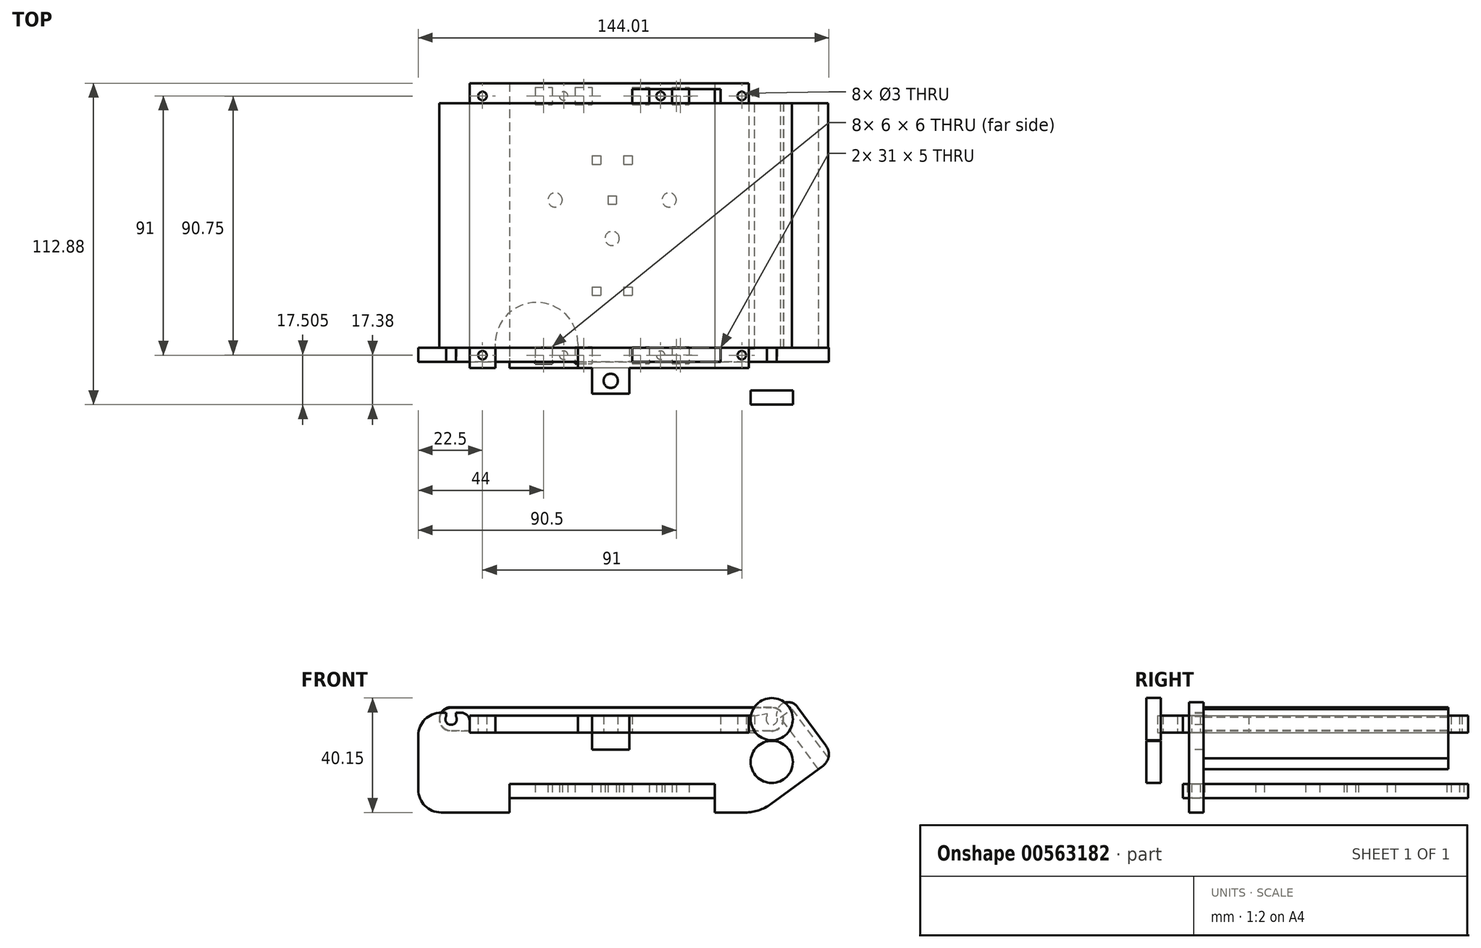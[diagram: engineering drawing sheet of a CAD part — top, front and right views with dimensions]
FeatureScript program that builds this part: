
annotation { "Feature Type Name" : "Feature", "Feature Type Description" : "" }
export const myFeature = defineFeature(function(context is Context, id is Id, definition is map)
    precondition{}
    {
        {
            var Q0;
            Q0=qCreatedBy(makeId("Top.planeOp"),FACE);
            var sketch = newSketch(context, id + "F0", { "sketchPlane" : qUnion([Q0])});
            skLineSegment(sketch, "E0.bottom", {"start": v(36, 50) * mm, "end": v(-36, 50) * mm});
            skLineSegment(sketch, "E0.top", {"start": v(36, -50) * mm, "end": v(-36, -50) * mm});
            skLineSegment(sketch, "E0.left", {"start": v(36, 50) * mm, "end": v(36, -50) * mm});
            skLineSegment(sketch, "E0.right", {"start": v(-36, 50) * mm, "end": v(-36, -50) * mm});
            skPoint(sketch, "E0.middle", {"position": v(0, 0) * mm});
            skLineSegment(sketch, "E1.bottom", {"start": v(-27, -42.5) * mm, "end": v(-21, -42.5) * mm});
            skLineSegment(sketch, "E1.top", {"start": v(-27, -48.5) * mm, "end": v(-21, -48.5) * mm});
            skLineSegment(sketch, "E1.left", {"start": v(-27, -42.5) * mm, "end": v(-27, -48.5) * mm});
            skLineSegment(sketch, "E1.right", {"start": v(-21, -42.5) * mm, "end": v(-21, -48.5) * mm});
            skLineSegment(sketch, "E2.bottom", {"start": v(-13, -42.5) * mm, "end": v(-7, -42.5) * mm});
            skLineSegment(sketch, "E2.top", {"start": v(-13, -48.5) * mm, "end": v(-7, -48.5) * mm});
            skLineSegment(sketch, "E2.left", {"start": v(-13, -42.5) * mm, "end": v(-13, -48.5) * mm});
            skLineSegment(sketch, "E2.right", {"start": v(-7, -42.5) * mm, "end": v(-7, -48.5) * mm});
            skLineSegment(sketch, "E3", {"start": v(-21, -45.5) * mm, "end": v(-17, -45.5) * mm, "construction": true});
            skLineSegment(sketch, "E4", {"start": v(-17, -45.5) * mm, "end": v(-13, -45.5) * mm, "construction": true});
            skCircle(sketch, "E5", {"center": v(-17, -45.5) * mm, "radius": 1.5 * mm});
            skLineSegment(sketch, "E6.bottom", {"start": v(-27, 48.5) * mm, "end": v(-21, 48.5) * mm});
            skLineSegment(sketch, "E6.top", {"start": v(-27, 42.5) * mm, "end": v(-21, 42.5) * mm});
            skLineSegment(sketch, "E6.left", {"start": v(-27, 48.5) * mm, "end": v(-27, 42.5) * mm});
            skLineSegment(sketch, "E6.right", {"start": v(-21, 48.5) * mm, "end": v(-21, 42.5) * mm});
            skLineSegment(sketch, "E7.bottom", {"start": v(-13, 48.5) * mm, "end": v(-7, 48.5) * mm});
            skLineSegment(sketch, "E7.top", {"start": v(-13, 42.5) * mm, "end": v(-7, 42.5) * mm});
            skLineSegment(sketch, "E7.left", {"start": v(-13, 48.5) * mm, "end": v(-13, 42.5) * mm});
            skLineSegment(sketch, "E7.right", {"start": v(-7, 48.5) * mm, "end": v(-7, 42.5) * mm});
            skLineSegment(sketch, "E8.bottom", {"start": v(7, 48.5) * mm, "end": v(13, 48.5) * mm});
            skLineSegment(sketch, "E8.top", {"start": v(7, 42.5) * mm, "end": v(13, 42.5) * mm});
            skLineSegment(sketch, "E8.left", {"start": v(7, 48.5) * mm, "end": v(7, 42.5) * mm});
            skLineSegment(sketch, "E8.right", {"start": v(13, 48.5) * mm, "end": v(13, 42.5) * mm});
            skLineSegment(sketch, "E9.bottom", {"start": v(21, 48.5) * mm, "end": v(27, 48.5) * mm});
            skLineSegment(sketch, "E9.top", {"start": v(21, 42.5) * mm, "end": v(27, 42.5) * mm});
            skLineSegment(sketch, "E9.left", {"start": v(21, 48.5) * mm, "end": v(21, 42.5) * mm});
            skLineSegment(sketch, "E9.right", {"start": v(27, 48.5) * mm, "end": v(27, 42.5) * mm});
            skLineSegment(sketch, "E10.bottom", {"start": v(7, -42.5) * mm, "end": v(13, -42.5) * mm});
            skLineSegment(sketch, "E10.top", {"start": v(7, -48.5) * mm, "end": v(13, -48.5) * mm});
            skLineSegment(sketch, "E10.left", {"start": v(7, -42.5) * mm, "end": v(7, -48.5) * mm});
            skLineSegment(sketch, "E10.right", {"start": v(13, -42.5) * mm, "end": v(13, -48.5) * mm});
            skLineSegment(sketch, "E11.bottom", {"start": v(21, -42.5) * mm, "end": v(27, -42.5) * mm});
            skLineSegment(sketch, "E11.top", {"start": v(21, -48.5) * mm, "end": v(27, -48.5) * mm});
            skLineSegment(sketch, "E11.left", {"start": v(21, -42.5) * mm, "end": v(21, -48.5) * mm});
            skLineSegment(sketch, "E11.right", {"start": v(27, -42.5) * mm, "end": v(27, -48.5) * mm});
            skLineSegment(sketch, "E12", {"start": v(-21, 45.5) * mm, "end": v(-17, 45.5) * mm, "construction": true});
            skLineSegment(sketch, "E13", {"start": v(-17, 45.5) * mm, "end": v(-13, 45.5) * mm, "construction": true});
            skLineSegment(sketch, "E14", {"start": v(13, 45.5) * mm, "end": v(17, 45.5) * mm, "construction": true});
            skLineSegment(sketch, "E15", {"start": v(17, 45.5) * mm, "end": v(21, 45.5) * mm, "construction": true});
            skLineSegment(sketch, "E16", {"start": v(13, -45.5) * mm, "end": v(17, -45.5) * mm, "construction": true});
            skLineSegment(sketch, "E17", {"start": v(17, -45.5) * mm, "end": v(21, -45.5) * mm, "construction": true});
            skLineSegment(sketch, "E18", {"start": v(0, 0) * mm, "end": v(36, 0) * mm, "construction": true});
            skLineSegment(sketch, "E19", {"start": v(0, 0) * mm, "end": v(0, 50) * mm, "construction": true});
            skCircle(sketch, "E20", {"center": v(-17, 45.5) * mm, "radius": 1.5 * mm});
            skCircle(sketch, "E21", {"center": v(17, 45.5) * mm, "radius": 1.5 * mm});
            skCircle(sketch, "E22", {"center": v(17, -45.5) * mm, "radius": 1.5 * mm});
            skCircle(sketch, "E23", {"center": v(0, -4.5) * mm, "radius": 2.5 * mm});
            skCircle(sketch, "E24", {"center": v(20, 9) * mm, "radius": 2.5 * mm});
            skCircle(sketch, "E25", {"center": v(-20, 9) * mm, "radius": 2.5 * mm});
            skLineSegment(sketch, "E26", {"start": v(0, -4.5) * mm, "end": v(-20, 9) * mm, "construction": true});
            skLineSegment(sketch, "E27", {"start": v(20, 9) * mm, "end": v(-20, 9) * mm, "construction": true});
            skLineSegment(sketch, "E28", {"start": v(20, 9) * mm, "end": v(0, -4.5) * mm, "construction": true});
            skPoint(sketch, "E29", {"position": v(0, 9) * mm});
            skLineSegment(sketch, "E30.bottom", {"start": v(-7, -21.5) * mm, "end": v(-4, -21.5) * mm});
            skLineSegment(sketch, "E30.top", {"start": v(-7, -24.5) * mm, "end": v(-4, -24.5) * mm});
            skLineSegment(sketch, "E30.left", {"start": v(-7, -21.5) * mm, "end": v(-7, -24.5) * mm});
            skLineSegment(sketch, "E30.right", {"start": v(-4, -21.5) * mm, "end": v(-4, -24.5) * mm});
            skLineSegment(sketch, "E31.bottom", {"start": v(4, -21.5) * mm, "end": v(7, -21.5) * mm});
            skLineSegment(sketch, "E31.top", {"start": v(4, -24.5) * mm, "end": v(7, -24.5) * mm});
            skLineSegment(sketch, "E31.left", {"start": v(4, -21.5) * mm, "end": v(4, -24.5) * mm});
            skLineSegment(sketch, "E31.right", {"start": v(7, -21.5) * mm, "end": v(7, -24.5) * mm});
            skLineSegment(sketch, "E32.bottom", {"start": v(-1.5, 10.5) * mm, "end": v(1.5, 10.5) * mm});
            skLineSegment(sketch, "E32.top", {"start": v(-1.5, 7.5) * mm, "end": v(1.5, 7.5) * mm});
            skLineSegment(sketch, "E32.left", {"start": v(-1.5, 10.5) * mm, "end": v(-1.5, 7.5) * mm});
            skLineSegment(sketch, "E32.right", {"start": v(1.5, 10.5) * mm, "end": v(1.5, 7.5) * mm});
            skLineSegment(sketch, "E33.bottom", {"start": v(-7, 24.5) * mm, "end": v(-4, 24.5) * mm});
            skLineSegment(sketch, "E33.top", {"start": v(-7, 21.5) * mm, "end": v(-4, 21.5) * mm});
            skLineSegment(sketch, "E33.left", {"start": v(-7, 24.5) * mm, "end": v(-7, 21.5) * mm});
            skLineSegment(sketch, "E33.right", {"start": v(-4, 24.5) * mm, "end": v(-4, 21.5) * mm});
            skLineSegment(sketch, "E34.bottom", {"start": v(4, 24.5) * mm, "end": v(7, 24.5) * mm});
            skLineSegment(sketch, "E34.top", {"start": v(4, 21.5) * mm, "end": v(7, 21.5) * mm});
            skLineSegment(sketch, "E34.left", {"start": v(4, 24.5) * mm, "end": v(4, 21.5) * mm});
            skLineSegment(sketch, "E34.right", {"start": v(7, 24.5) * mm, "end": v(7, 21.5) * mm});
            skSolve(sketch);
        }
        {
            var Q0;
            Q0=makeQuery(id+"F0.imprint","IMPRINT",FACE,{"disambiguationData":[TD([[makeQuery(id+"F0.imprint","IMPRINT",EDGE,{"derivedFrom":sQuery(id+"F0.wireOp",EDGE,"E0.bottom")}),1.0]])]});
            extrude(context, id + "F1", {"entities" : qUnion([Q0]), "depth" : 5 * mm, "offsetDistance" : 25 * mm});
        }
        {
            var Q0;
            Q0=qCreatedBy(makeId("Top.planeOp"),FACE);
            cPlane(context, id + "F2", {"entities" : qUnion([Q0]), "cplaneType" : CPlaneType.OFFSET, "offset" : 23 * mm, "width" : 150 * mm, "height" : 150 * mm});
        }
        {
            var Q0;
            Q0=qCreatedBy(id+"F2.planeOp",FACE);
            var sketch = newSketch(context, id + "F3", { "sketchPlane" : qUnion([Q0])});
            skLineSegment(sketch, "E35.bottom", {"start": v(-50, -50) * mm, "end": v(-41, -50) * mm});
            skLineSegment(sketch, "E35.top", {"start": v(-50, 50) * mm, "end": v(48, 50) * mm});
            skLineSegment(sketch, "E35.left", {"start": v(-50, -50) * mm, "end": v(-50, 50) * mm});
            skLineSegment(sketch, "E35.right", {"start": v(50, -43) * mm, "end": v(50, 43) * mm});
            skPoint(sketch, "E35.middle", {"position": v(0, 0) * mm});
            skLineSegment(sketch, "E36.bottom", {"start": v(-45.5, -45.5) * mm, "end": v(45.5, -45.5) * mm, "construction": true});
            skLineSegment(sketch, "E36.top", {"start": v(-45.5, 45.5) * mm, "end": v(45.5, 45.5) * mm, "construction": true});
            skLineSegment(sketch, "E36.left", {"start": v(-45.5, -45.5) * mm, "end": v(-45.5, 45.5) * mm, "construction": true});
            skLineSegment(sketch, "E36.right", {"start": v(45.5, -45.5) * mm, "end": v(45.5, 45.5) * mm, "construction": true});
            skCircle(sketch, "E37", {"center": v(-45.5, -45.5) * mm, "radius": 1.5 * mm});
            skCircle(sketch, "E38", {"center": v(-45.5, 45.5) * mm, "radius": 1.5 * mm});
            skCircle(sketch, "E39", {"center": v(45.5, -45.5) * mm, "radius": 1.5 * mm});
            skCircle(sketch, "E40", {"center": v(45.5, 45.5) * mm, "radius": 1.5 * mm});
            skLineSegment(sketch, "E41.bottom", {"start": v(7, -47.87) * mm, "end": v(38, -47.88) * mm});
            skLineSegment(sketch, "E41.top", {"start": v(7, -42.87) * mm, "end": v(38, -42.88) * mm});
            skLineSegment(sketch, "E41.left", {"start": v(7, -47.88) * mm, "end": v(7, -42.88) * mm});
            skLineSegment(sketch, "E41.right", {"start": v(38, -47.88) * mm, "end": v(38, -42.88) * mm});
            skLineSegment(sketch, "E42.bottom", {"start": v(7, 42.88) * mm, "end": v(38, 42.88) * mm});
            skLineSegment(sketch, "E42.top", {"start": v(7, 47.88) * mm, "end": v(38, 47.88) * mm});
            skLineSegment(sketch, "E42.left", {"start": v(7, 42.88) * mm, "end": v(7, 47.88) * mm});
            skLineSegment(sketch, "E42.right", {"start": v(38, 42.88) * mm, "end": v(38, 47.88) * mm});
            skLineSegment(sketch, "E43", {"start": v(45.5, 0) * mm, "end": v(-45.5, 0) * mm, "construction": true});
            skLineSegment(sketch, "E44", {"start": v(-41, -50) * mm, "end": v(-41, -41.5) * mm});
            skLineSegment(sketch, "E45", {"start": v(-41, -41.5) * mm, "end": v(-12, -41.5) * mm, "construction": true});
            skLineSegment(sketch, "E46", {"start": v(-12, -41.5) * mm, "end": v(-12, -50) * mm});
            skArc(sketch, "E47", {"start": v(-12, -41.5) * mm, "mid": v(-26.5, -27) * mm, "end": v(-41, -41.5) * mm});
            skLineSegment(sketch, "E48.trimOffspring", {"start": v(-12, -50) * mm, "end": v(-7, -50) * mm});
            skLineSegment(sketch, "E49", {"start": v(-7, -59) * mm, "end": v(6, -59) * mm});
            skLineSegment(sketch, "E50", {"start": v(6, -59) * mm, "end": v(6, -50) * mm});
            skLineSegment(sketch, "E51.trimOffspring", {"start": v(6, -50) * mm, "end": v(48, -50) * mm});
            skLineSegment(sketch, "E52", {"start": v(-7, -59) * mm, "end": v(-7, -50) * mm});
            skLineSegment(sketch, "E53", {"start": v(6, -54.5) * mm, "end": v(-0.5, -54.5) * mm, "construction": true});
            skLineSegment(sketch, "E54", {"start": v(-0.5, -54.5) * mm, "end": v(-0.5, -59) * mm, "construction": true});
            skCircle(sketch, "E55", {"center": v(-0.5, -54.5) * mm, "radius": 2.5 * mm});
            skLineSegment(sketch, "E56", {"start": v(48, -50) * mm, "end": v(48, -43) * mm});
            skLineSegment(sketch, "E57", {"start": v(48, -43) * mm, "end": v(50, -43) * mm});
            skLineSegment(sketch, "E58", {"start": v(50, 43) * mm, "end": v(48, 43) * mm});
            skLineSegment(sketch, "E59", {"start": v(48, 43) * mm, "end": v(48, 50) * mm});
            skPoint(sketch, "E60.orphan", {"position": v(50, -50) * mm});
            skPoint(sketch, "E61.orphan", {"position": v(50, 50) * mm});
            skSolve(sketch);
        }
        {
            var Q0;
            Q0=makeQuery(id+"F3.imprint","IMPRINT",FACE,{"disambiguationData":[TD([[makeQuery(id+"F3.imprint","IMPRINT",EDGE,{"derivedFrom":sQuery(id+"F3.wireOp",EDGE,"E35.bottom")}),1.0]])]});
            extrude(context, id + "F4", {"entities" : qUnion([Q0]), "depth" : 6 * mm, "offsetDistance" : 25 * mm});
        }
        {
            var Q0;
            Q0=makeQuery(id+"F1.opExtrude","SWEPT_FACE",FACE,{"disambiguationData":[OSD([sQuery(id+"F0.wireOp",EDGE,"E0.top")])]});
            var Q1;
            Q1=makeQuery(id+"F4.opExtrude","CAP_VERTEX",VERTEX,{"disambiguationData":[OSD([sQuery(id+"F3.wireOp",EDGE,"E41.bottom"),sQuery(id+"F3.wireOp",EDGE,"E41.left")])],"isStart":true});
            cPlane(context, id + "F5", {"entities" : qUnion([Q0, Q1]), "cplaneType" : CPlaneType.PLANE_POINT, "offset" : 25 * mm, "width" : 150 * mm, "height" : 150 * mm});
        }
        {
            var Q0;
            Q0=qCreatedBy(id+"F5.planeOp",FACE);
            var sketch = newSketch(context, id + "F6", { "sketchPlane" : qUnion([Q0])});
            skLineSegment(sketch, "E62", {"start": v(36, -5) * mm, "end": v(36, 5) * mm});
            skLineSegment(sketch, "E63", {"start": v(36, 5) * mm, "end": v(-36, 5) * mm});
            skLineSegment(sketch, "E64", {"start": v(-36, 5) * mm, "end": v(-36, -5) * mm});
            skLineSegment(sketch, "E65", {"start": v(-36, -5) * mm, "end": v(-68, -5) * mm});
            skLineSegment(sketch, "E66", {"start": v(-68, -5) * mm, "end": v(-68, 30) * mm});
            skLineSegment(sketch, "E67", {"start": v(-68, 30) * mm, "end": v(-58.25, 30) * mm});
            skLineSegment(sketch, "E68", {"start": v(-50, 30) * mm, "end": v(-50, 23) * mm});
            skLineSegment(sketch, "E69", {"start": v(-50, 23) * mm, "end": v(-7, 23) * mm});
            skLineSegment(sketch, "E70", {"start": v(-7, 23) * mm, "end": v(-7, 17) * mm});
            skLineSegment(sketch, "E71", {"start": v(-7, 17) * mm, "end": v(6, 17) * mm});
            skLineSegment(sketch, "E72", {"start": v(6, 17) * mm, "end": v(6, 23) * mm});
            skLineSegment(sketch, "E73", {"start": v(6, 23) * mm, "end": v(48, 23) * mm});
            skLineSegment(sketch, "E74", {"start": v(48, 23) * mm, "end": v(48, 28.66) * mm});
            skLineSegment(sketch, "E75", {"start": v(57.75, 28.72) * mm, "end": v(57.75, 29.72) * mm});
            skLineSegment(sketch, "E76", {"start": v(64.97, 32.09) * mm, "end": v(78, 14.36) * mm});
            skLineSegment(sketch, "E77", {"start": v(78, 14.36) * mm, "end": v(51.65, -5) * mm});
            skLineSegment(sketch, "E78", {"start": v(51.65, -5) * mm, "end": v(36, -5) * mm});
            skLineSegment(sketch, "E79", {"start": v(48, 28.66) * mm, "end": v(54.25, 29.72) * mm});
            skLineSegment(sketch, "E80", {"start": v(54.25, 29.72) * mm, "end": v(54.25, 28.72) * mm});
            skArc(sketch, "E81", {"start": v(54.25, 28.72) * mm, "mid": v(56, 25.75) * mm, "end": v(57.75, 28.72) * mm});
            skLineSegment(sketch, "E82", {"start": v(56, 27.75) * mm, "end": v(56, 28.75) * mm, "construction": true});
            skArc(sketch, "E83", {"start": v(64.97, 32.09) * mm, "mid": v(60.5, 33.52) * mm, "end": v(57.75, 29.72) * mm});
            skLineSegment(sketch, "E84", {"start": v(54.25, 29.72) * mm, "end": v(57.75, 29.72) * mm, "construction": true});
            skArc(sketch, "E85", {"start": v(-58.25, 28.72) * mm, "mid": v(-56.5, 25.75) * mm, "end": v(-54.75, 28.72) * mm});
            skLineSegment(sketch, "E86", {"start": v(-58.25, 28.72) * mm, "end": v(-58.25, 30) * mm});
            skLineSegment(sketch, "E87", {"start": v(-54.75, 28.72) * mm, "end": v(-54.75, 30) * mm});
            skLineSegment(sketch, "E88", {"start": v(-56.5, 27.75) * mm, "end": v(-56.5, 30) * mm, "construction": true});
            skLineSegment(sketch, "E89.trimOffspring", {"start": v(-54.75, 30) * mm, "end": v(-50, 30) * mm});
            skLineSegment(sketch, "E90", {"start": v(-58.25, 30) * mm, "end": v(-54.75, 30) * mm, "construction": true});
            skLineSegment(sketch, "E91", {"start": v(56, 27.75) * mm, "end": v(-56.5, 27.75) * mm, "construction": true});
            skLineSegment(sketch, "E92", {"start": v(54.25, 28.72) * mm, "end": v(57.75, 28.72) * mm, "construction": true});
            skSolve(sketch);
        }
        {
            var Q0;
            Q0 = qSketchRegion(id + "F6", true);
            extrude(context, id + "F7", {"entities" : qUnion([Q0]), "oppositeDirection" : true, "depth" : 5 * mm, "offsetDistance" : 25 * mm});
        }
        {
            var Q0;
            Q0=makeQuery(id+"F7.opExtrude","SWEPT_EDGE",EDGE,{"disambiguationData":[OSD([sQuery(id+"F6.wireOp",EDGE,"E76"),sQuery(id+"F6.wireOp",EDGE,"E77")])]});
            fillet(context, id + "F8", {"entities" : qUnion([Q0]), "tangentPropagation" : true, "radius" : 5 * mm, "defaultsChanged" : false, "vertexSettings" : [], "allowEdgeOverflow" : false});
        }
        {
            var Q0;
            Q0=makeQuery(id+"F7.opExtrude","SWEPT_EDGE",EDGE,{"disambiguationData":[OSD([sQuery(id+"F6.wireOp",EDGE,"E77"),sQuery(id+"F6.wireOp",EDGE,"E78")])]});
            fillet(context, id + "F9", {"entities" : qUnion([Q0]), "tangentPropagation" : true, "radius" : 15 * mm, "defaultsChanged" : true, "vertexSettings" : [], "allowEdgeOverflow" : false});
        }
        {
            var Q0;
            Q0=makeQuery(id+"F7.opExtrude","SWEPT_EDGE",EDGE,{"disambiguationData":[OSD([sQuery(id+"F6.wireOp",EDGE,"E65"),sQuery(id+"F6.wireOp",EDGE,"E66")])]});
            var Q1;
            Q1=makeQuery(id+"F7.opExtrude","SWEPT_EDGE",EDGE,{"disambiguationData":[OSD([sQuery(id+"F6.wireOp",EDGE,"E66"),sQuery(id+"F6.wireOp",EDGE,"E67")])]});
            fillet(context, id + "F10", {"entities" : qUnion([Q0, Q1]), "tangentPropagation" : true, "radius" : 8 * mm, "defaultsChanged" : false, "vertexSettings" : [], "allowEdgeOverflow" : false});
        }
        {
            var Q0;
            Q0=makeQuery(id+"F7.opExtrude","SWEPT_EDGE",EDGE,{"disambiguationData":[OSD([sQuery(id+"F6.wireOp",EDGE,"E68"),sQuery(id+"F6.wireOp",EDGE,"E89.trimOffspring")])]});
            fillet(context, id + "F11", {"entities" : qUnion([Q0]), "tangentPropagation" : true, "radius" : 3 * mm, "defaultsChanged" : true, "vertexSettings" : [], "allowEdgeOverflow" : false});
        }
        {
            var Q0;
            Q0=makeQuery(id+"F7.opExtrude","CAP_FACE",FACE,{"disambiguationData":[OSD([sQuery(id+"F6.wireOp",EDGE,"E62"),sQuery(id+"F6.wireOp",EDGE,"E63"),sQuery(id+"F6.wireOp",EDGE,"E64"),sQuery(id+"F6.wireOp",EDGE,"E65"),sQuery(id+"F6.wireOp",EDGE,"E66"),sQuery(id+"F6.wireOp",EDGE,"E67"),sQuery(id+"F6.wireOp",EDGE,"E68"),sQuery(id+"F6.wireOp",EDGE,"E69"),sQuery(id+"F6.wireOp",EDGE,"E70"),sQuery(id+"F6.wireOp",EDGE,"E71"),sQuery(id+"F6.wireOp",EDGE,"E72"),sQuery(id+"F6.wireOp",EDGE,"E73"),sQuery(id+"F6.wireOp",EDGE,"E74"),sQuery(id+"F6.wireOp",EDGE,"E75"),sQuery(id+"F6.wireOp",EDGE,"E76"),sQuery(id+"F6.wireOp",EDGE,"E77"),sQuery(id+"F6.wireOp",EDGE,"E78"),sQuery(id+"F6.wireOp",EDGE,"E79"),sQuery(id+"F6.wireOp",EDGE,"E80"),sQuery(id+"F6.wireOp",EDGE,"E81"),sQuery(id+"F6.wireOp",EDGE,"E83"),sQuery(id+"F6.wireOp",EDGE,"E85"),sQuery(id+"F6.wireOp",EDGE,"E86"),sQuery(id+"F6.wireOp",EDGE,"E87"),sQuery(id+"F6.wireOp",EDGE,"E89.trimOffspring")])],"isStart":false});
            var sketch = newSketch(context, id + "F12", { "sketchPlane" : qUnion([Q0])});
            skLineSegment(sketch, "E93", {"start": v(-76.39, 13.17) * mm, "end": v(-63.07, 31.3) * mm});
            skLineSegment(sketch, "E94", {"start": v(-63.07, 31.3) * mm, "end": v(-59.04, 28.34) * mm});
            skLineSegment(sketch, "E95", {"start": v(-59.04, 28.34) * mm, "end": v(-72.36, 10.21) * mm});
            skLineSegment(sketch, "E96", {"start": v(-72.36, 10.21) * mm, "end": v(-76.39, 13.17) * mm});
            skSolve(sketch);
        }
        {
            var Q0;
            {var subQ8=sQuery(id+"F12.wireOp",EDGE,"E94");Q0=makeQuery(id+"F12.imprint","IMPRINT",FACE,{"disambiguationData":[TD([[makeQuery(id+"F12.imprint","IMPRINT",EDGE,{"derivedFrom":subQ8}),-1.0]])]});}
            var Q1;
            Q1=makeQuery(id+"F4.opExtrude","SWEPT_FACE",FACE,{"disambiguationData":[OSD([sQuery(id+"F3.wireOp",EDGE,"E58")])]});
            extrude(context, id + "F13", {"entities" : qUnion([Q0]), "endBound" : BoundingType.UP_TO_SURFACE, "depth" : 25 * mm, "endBoundEntityFace" : qUnion([Q1]), "offsetDistance" : 25 * mm});
        }
        {
            var Q0;
            Q0=makeQuery(id+"F7.opExtrude","CAP_FACE",FACE,{"disambiguationData":[OSD([sQuery(id+"F6.wireOp",EDGE,"E62"),sQuery(id+"F6.wireOp",EDGE,"E63"),sQuery(id+"F6.wireOp",EDGE,"E64"),sQuery(id+"F6.wireOp",EDGE,"E65"),sQuery(id+"F6.wireOp",EDGE,"E66"),sQuery(id+"F6.wireOp",EDGE,"E67"),sQuery(id+"F6.wireOp",EDGE,"E68"),sQuery(id+"F6.wireOp",EDGE,"E69"),sQuery(id+"F6.wireOp",EDGE,"E70"),sQuery(id+"F6.wireOp",EDGE,"E71"),sQuery(id+"F6.wireOp",EDGE,"E72"),sQuery(id+"F6.wireOp",EDGE,"E73"),sQuery(id+"F6.wireOp",EDGE,"E74"),sQuery(id+"F6.wireOp",EDGE,"E75"),sQuery(id+"F6.wireOp",EDGE,"E76"),sQuery(id+"F6.wireOp",EDGE,"E77"),sQuery(id+"F6.wireOp",EDGE,"E78"),sQuery(id+"F6.wireOp",EDGE,"E79"),sQuery(id+"F6.wireOp",EDGE,"E80"),sQuery(id+"F6.wireOp",EDGE,"E81"),sQuery(id+"F6.wireOp",EDGE,"E83"),sQuery(id+"F6.wireOp",EDGE,"E85"),sQuery(id+"F6.wireOp",EDGE,"E86"),sQuery(id+"F6.wireOp",EDGE,"E87"),sQuery(id+"F6.wireOp",EDGE,"E89.trimOffspring")])],"isStart":false});
            var sketch = newSketch(context, id + "F14", { "sketchPlane" : qUnion([Q0])});
            skArc(sketch, "E97", {"start": v(-56, 31.75) * mm, "mid": v(-60, 27.75) * mm, "end": v(-56, 23.75) * mm});
            skArc(sketch, "E98", {"start": v(56.5, 23.75) * mm, "mid": v(60.5, 27.75) * mm, "end": v(56.5, 31.75) * mm});
            skLineSegment(sketch, "E99", {"start": v(-56, 31.75) * mm, "end": v(56.5, 31.75) * mm});
            skLineSegment(sketch, "E100", {"start": v(-56, 23.75) * mm, "end": v(56.5, 23.75) * mm});
            skLineSegment(sketch, "E101", {"start": v(-56, 31.95) * mm, "end": v(56.5, 31.95) * mm});
            skLineSegment(sketch, "E102", {"start": v(56.5, 31.95) * mm, "end": v(56.5, 23.55) * mm, "construction": true});
            skLineSegment(sketch, "E103", {"start": v(56.5, 23.55) * mm, "end": v(-56, 23.55) * mm});
            skLineSegment(sketch, "E104", {"start": v(-56, 23.55) * mm, "end": v(-56, 31.95) * mm, "construction": true});
            skLineSegment(sketch, "E105", {"start": v(-56, 27.75) * mm, "end": v(56.5, 27.75) * mm, "construction": true});
            skArc(sketch, "E106", {"start": v(-56, 31.95) * mm, "mid": v(-60.2, 27.75) * mm, "end": v(-56, 23.55) * mm});
            skArc(sketch, "E107", {"start": v(56.5, 23.55) * mm, "mid": v(60.7, 27.75) * mm, "end": v(56.5, 31.95) * mm});
            skSolve(sketch);
        }
        {
            var Q0;
            {var subQ0=sQuery(id+"F14.wireOp",EDGE,"E99");Q0=makeQuery(id+"F14.imprint","IMPRINT",FACE,{"disambiguationData":[TD([[makeQuery(id+"F14.imprint","IMPRINT",EDGE,{"derivedFrom":subQ0}),1.0]])]});}
            var Q1;
            {var subQ10=sQuery(id+"F14.wireOp",EDGE,"E100");var subQ12=sQuery(id+"F14.wireOp",EDGE,"E98");var subQ13=makeQuery(id+"F14.imprint","INTERSECT",VERTEX,{"derivedFrom":[subQ12,subQ10]});Q1=makeQuery(id+"F14.imprint","IMPRINT",FACE,{"disambiguationData":[TD([[makeQuery(id+"F14.imprint","IMPRINT",EDGE,{"disambiguationData":[TD([[subQ13,-1.0]])],"derivedFrom":subQ12}),-1.0]])]});}
            var Q2;
            {var subQ5=sQuery(id+"F14.wireOp",EDGE,"E97");var subQ7=sQuery(id+"F14.wireOp",EDGE,"E100");var subQ8=makeQuery(id+"F14.imprint","INTERSECT",VERTEX,{"derivedFrom":[subQ5,subQ7]});Q2=makeQuery(id+"F14.imprint","IMPRINT",FACE,{"disambiguationData":[TD([[makeQuery(id+"F14.imprint","IMPRINT",EDGE,{"disambiguationData":[TD([[subQ8,1.0]])],"derivedFrom":subQ5}),-1.0]])]});}
            var Q3;
            Q3=makeQuery(id+"F4.opExtrude","SWEPT_FACE",FACE,{"disambiguationData":[OSD([sQuery(id+"F3.wireOp",EDGE,"E58")])]});
            extrude(context, id + "F15", {"entities" : qUnion([Q0, Q1, Q2]), "endBound" : BoundingType.UP_TO_SURFACE, "depth" : 25 * mm, "endBoundEntityFace" : qUnion([Q3]), "offsetDistance" : 25 * mm});
        }
        {
            var Q0;
            Q0=makeQuery(id+"F7.opExtrude","CAP_FACE",FACE,{"disambiguationData":[OSD([sQuery(id+"F6.wireOp",EDGE,"E62"),sQuery(id+"F6.wireOp",EDGE,"E63"),sQuery(id+"F6.wireOp",EDGE,"E64"),sQuery(id+"F6.wireOp",EDGE,"E65"),sQuery(id+"F6.wireOp",EDGE,"E66"),sQuery(id+"F6.wireOp",EDGE,"E67"),sQuery(id+"F6.wireOp",EDGE,"E68"),sQuery(id+"F6.wireOp",EDGE,"E69"),sQuery(id+"F6.wireOp",EDGE,"E70"),sQuery(id+"F6.wireOp",EDGE,"E71"),sQuery(id+"F6.wireOp",EDGE,"E72"),sQuery(id+"F6.wireOp",EDGE,"E73"),sQuery(id+"F6.wireOp",EDGE,"E74"),sQuery(id+"F6.wireOp",EDGE,"E75"),sQuery(id+"F6.wireOp",EDGE,"E76"),sQuery(id+"F6.wireOp",EDGE,"E77"),sQuery(id+"F6.wireOp",EDGE,"E78"),sQuery(id+"F6.wireOp",EDGE,"E79"),sQuery(id+"F6.wireOp",EDGE,"E80"),sQuery(id+"F6.wireOp",EDGE,"E81"),sQuery(id+"F6.wireOp",EDGE,"E83"),sQuery(id+"F6.wireOp",EDGE,"E85"),sQuery(id+"F6.wireOp",EDGE,"E86"),sQuery(id+"F6.wireOp",EDGE,"E87"),sQuery(id+"F6.wireOp",EDGE,"E89.trimOffspring")])],"isStart":true});
            cPlane(context, id + "F16", {"entities" : qUnion([Q0]), "cplaneType" : CPlaneType.OFFSET, "offset" : 15 * mm, "width" : 150 * mm, "height" : 150 * mm});
        }
        {
            var Q0;
            Q0=qCreatedBy(id+"F16.planeOp",FACE);
            var sketch = newSketch(context, id + "F17", { "sketchPlane" : qUnion([Q0])});
            skCircle(sketch, "E108", {"center": v(56, 27.75) * mm, "radius": 7.4 * mm});
            skCircle(sketch, "E109", {"center": v(56, 12.75) * mm, "radius": 7.4 * mm});
            skLineSegment(sketch, "E110", {"start": v(56, 27.75) * mm, "end": v(56, 12.75) * mm, "construction": true});
            skSolve(sketch);
        }
        {
            var Q0;
            Q0=makeQuery(id+"F17.imprint","IMPRINT",FACE,{"disambiguationData":[TD([[makeQuery(id+"F17.imprint","IMPRINT",EDGE,{"derivedFrom":sQuery(id+"F17.wireOp",EDGE,"E108")}),1.0]])]});
            var Q1;
            Q1=makeQuery(id+"F17.imprint","IMPRINT",FACE,{"disambiguationData":[TD([[makeQuery(id+"F17.imprint","IMPRINT",EDGE,{"derivedFrom":sQuery(id+"F17.wireOp",EDGE,"E109")}),1.0]])]});
            extrude(context, id + "F18", {"entities" : qUnion([Q0, Q1]), "oppositeDirection" : true, "depth" : 5 * mm, "offsetDistance" : 25 * mm});
        }
    });
